# Revit family: 94728104
name_source: partatom
category: Modelos genéricos
revit_build: Autodesk Revit 2016 (Build: 20150220_1215(x64)
units: mm (PartAtom-declared; Revit-internal decimal feet)

## family parameters
Com base no plano de trabalho = Não
Compartilhado = Não
Corte com vazios quando carregados = Não
Cota do conector redondo = Utilizar diâmetro
Pode hospedar o vergalhão = Não
Ponto de cálculo do ambiente = Não
Sempre na vertical = Sim
Tipo de parte = Normal

## types (2) — shared parameters
Comentários de tipos = *ler manual de instruções para instalação*
Consumo máximo = 11,60 kWh
Código de montagem = 94728/104
Descrição = 94728/104
Desenvolvedor = Factory Cursos & Desenvolvimento
Fabricante = Tramontina
Peso Bruto = 28,6 kg
Peso Líquido = 23,6 kg
Potência Máxima - Auxliar = 1,00 kW
Potência Máxima - Rápido = 3,00 kW
Potência Máxima - Semirápido (2X) = 1,75 kW
Potência Máxima - Tripla Chama = 4,10 kW
Potência elétrica = 2 W
Site do desenvolvedor = www.factorycursos.com.br
URL = www.tramontina.com.br

## per-type parameters (varying)
| type | Frequência | Modelo | Tensão |
| Tramontina - Penta Glass Flatt 5GX 90 - 127 V | 50 Hz | Tramontina - Penta Glass Flatt 5GX 90 | 127 V |
| Tramontina - Penta Inox 5GX 90 Safestop | 60 Hz | Tramontina TDC - Tramontina - Penta Inox 5GX 90 Safestop | 220 V |
